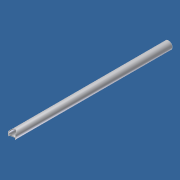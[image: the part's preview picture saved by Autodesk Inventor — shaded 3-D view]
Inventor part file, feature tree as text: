
AUTODESK INVENTOR PART (.ipt)
format: ipt  version: 2012 (Build 160160000, 160)  size: 89,600 bytes
history: native  units: in
note: dims shown in document units (in); Inventor stores cm internally (conversion verified against a paired STEP export)
features: other x4, sketch x2
ambient origin geometry x8: Origin, YZ Plane, XZ Plane, XY Plane, X Axis, Y Axis, Z Axis, Center Point
bodies: Solid1 (feature_tree)
feature tree (6):
  other  "GE-12057-01.ipt"
  other  "Solid1::GE-12057-01.ipt"
  sketch  "Sketch1"  dims[d0=0.3937in]
  sketch  "Sketch2"
  other  "Work Axis1"
  other  "TaggingFeature1"
